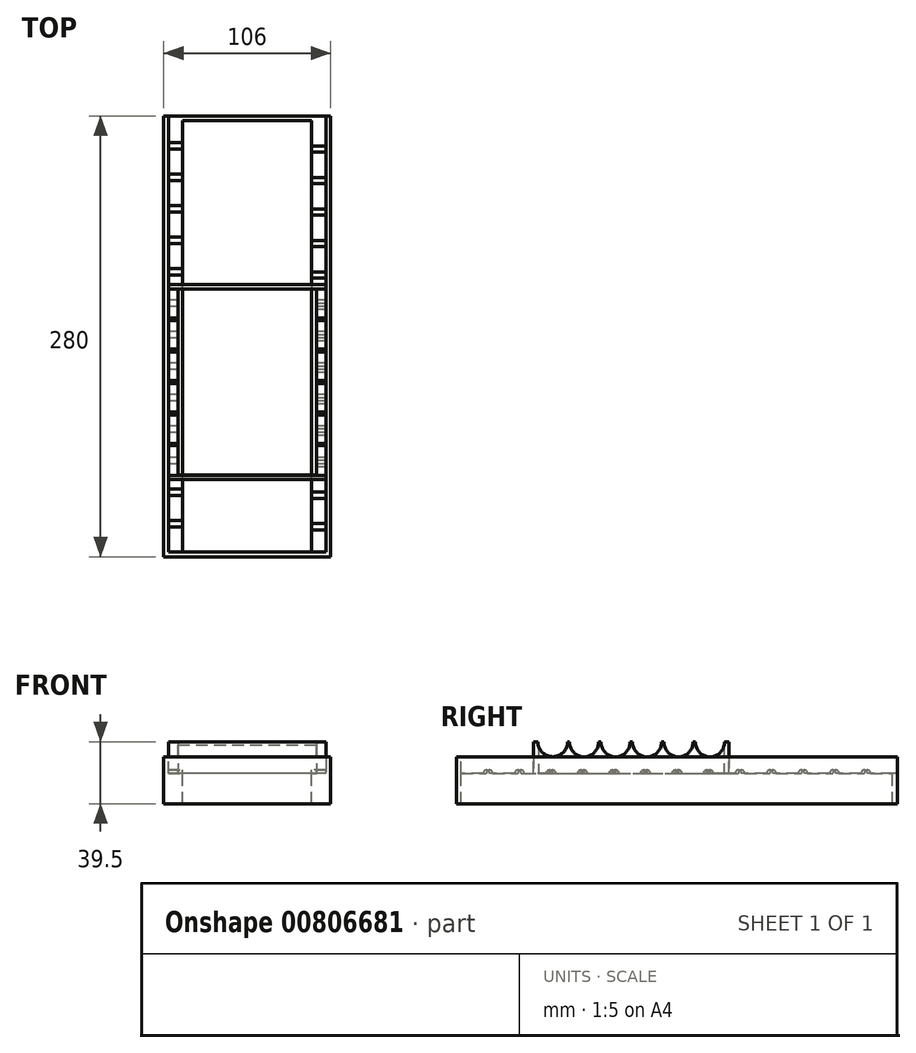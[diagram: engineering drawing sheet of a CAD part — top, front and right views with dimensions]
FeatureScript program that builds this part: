
annotation { "Feature Type Name" : "Feature", "Feature Type Description" : "" }
export const myFeature = defineFeature(function(context is Context, id is Id, definition is map)
    precondition{}
    {
        {
            var Q0;
            Q0=qCreatedBy(makeId("Top.planeOp"),FACE);
            var sketch = newSketch(context, id + "F0", { "sketchPlane" : qUnion([Q0])});
            skPoint(sketch, "E0.middle", {"position": v(0, 0) * mm});
            skLineSegment(sketch, "E1.bottom", {"start": v(-53, 140) * mm, "end": v(53, 140) * mm});
            skLineSegment(sketch, "E1.top", {"start": v(-53, -140) * mm, "end": v(53, -140) * mm});
            skLineSegment(sketch, "E1.left", {"start": v(-53, 140) * mm, "end": v(-53, -140) * mm});
            skLineSegment(sketch, "E1.right", {"start": v(53, 140) * mm, "end": v(53, -140) * mm});
            skSolve(sketch);
        }
        {
            var Q0;
            Q0 = qSketchRegion(id + "F0", true);
            extrude(context, id + "F1", {"entities" : qUnion([Q0]), "endBound" : BoundingType.SYMMETRIC, "depth" : 30 * mm, "offsetDistance" : 25 * mm});
        }
        {
            var Q0;
            Q0=makeQuery(id+"F1.opExtrude","CAP_FACE",FACE,{"disambiguationData":[OSD([sQuery(id+"F0.wireOp",EDGE,"E1.bottom"),sQuery(id+"F0.wireOp",EDGE,"E1.top"),sQuery(id+"F0.wireOp",EDGE,"E1.left"),sQuery(id+"F0.wireOp",EDGE,"E1.right")])],"isStart":false});
            var sketch = newSketch(context, id + "F2", { "sketchPlane" : qUnion([Q0])});
            skLineSegment(sketch, "E2.bottom", {"start": v(-41, 137) * mm, "end": v(41, 137) * mm});
            skLineSegment(sketch, "E2.top", {"start": v(-41, -137) * mm, "end": v(41, -137) * mm});
            skLineSegment(sketch, "E2.left", {"start": v(-41, 137) * mm, "end": v(-41, -137) * mm});
            skLineSegment(sketch, "E2.right", {"start": v(41, 137) * mm, "end": v(41, -137) * mm});
            skPoint(sketch, "E2.middle", {"position": v(0, 0) * mm});
            skSolve(sketch);
        }
        {
            var Q0;
            Q0=makeQuery(id+"F2.imprint","IMPRINT",FACE,{"disambiguationData":[TD([[makeQuery(id+"F2.imprint","IMPRINT",EDGE,{"derivedFrom":sQuery(id+"F2.wireOp",EDGE,"E2.bottom")}),-1.0]])]});
            extrude(context, id + "F3", {"entities" : qUnion([Q0]), "operationType" : NewBodyOperationType.REMOVE, "oppositeDirection" : true, "depth" : 39 * mm, "offsetDistance" : 25 * mm});
        }
        {
            var Q0;
            Q0=makeQuery(id+"F3.boolean.opBoolean","COPY",FACE,{"derivedFrom":makeQuery(id+"F3.opExtrude","SWEPT_FACE",FACE,{"disambiguationData":[OSD([sQuery(id+"F2.wireOp",EDGE,"E2.left")])]})});
            var sketch = newSketch(context, id + "F4", { "sketchPlane" : qUnion([Q0])});
            skLineSegment(sketch, "E3.bottom", {"start": v(-137, 15) * mm, "end": v(137, 15) * mm});
            skPoint(sketch, "E3.middle", {"position": v(0, 0) * mm});
            skLineSegment(sketch, "E4.left", {"start": v(-137, 15) * mm, "end": v(-137, 4.5) * mm});
            skLineSegment(sketch, "E4.right", {"start": v(137, 15) * mm, "end": v(137, 4.5) * mm});
            skLineSegment(sketch, "E5", {"start": v(-137, 4.5) * mm, "end": v(-121, 4.5) * mm});
            skArc(sketch, "E6", {"start": v(-117, 4.5) * mm, "mid": v(-119, 6.5) * mm, "end": v(-121, 4.5) * mm});
            skLineSegment(sketch, "E7", {"start": v(-117, 4.5) * mm, "end": v(-101, 4.5) * mm});
            skArc(sketch, "E8", {"start": v(-97, 4.5) * mm, "mid": v(-99, 6.5) * mm, "end": v(-101, 4.5) * mm});
            skLineSegment(sketch, "E9", {"start": v(-97, 4.5) * mm, "end": v(-81, 4.5) * mm});
            skArc(sketch, "E10", {"start": v(-77, 4.5) * mm, "mid": v(-79, 6.5) * mm, "end": v(-81, 4.5) * mm});
            skLineSegment(sketch, "E11", {"start": v(-77, 4.5) * mm, "end": v(-61, 4.5) * mm});
            skArc(sketch, "E12", {"start": v(-57, 4.5) * mm, "mid": v(-59, 6.5) * mm, "end": v(-61, 4.5) * mm});
            skLineSegment(sketch, "E13", {"start": v(-57, 4.5) * mm, "end": v(-41, 4.5) * mm});
            skArc(sketch, "E14", {"start": v(-37, 4.5) * mm, "mid": v(-39, 6.5) * mm, "end": v(-41, 4.5) * mm});
            skLineSegment(sketch, "E15", {"start": v(-37, 4.5) * mm, "end": v(-21, 4.5) * mm});
            skArc(sketch, "E16", {"start": v(-17, 4.5) * mm, "mid": v(-19, 6.5) * mm, "end": v(-21, 4.5) * mm});
            skLineSegment(sketch, "E17", {"start": v(-17, 4.5) * mm, "end": v(-1, 4.5) * mm});
            skArc(sketch, "E18", {"start": v(3, 4.5) * mm, "mid": v(1, 6.5) * mm, "end": v(-1, 4.5) * mm});
            skLineSegment(sketch, "E19", {"start": v(3, 4.5) * mm, "end": v(19, 4.5) * mm});
            skArc(sketch, "E20", {"start": v(23, 4.5) * mm, "mid": v(21, 6.5) * mm, "end": v(19, 4.5) * mm});
            skLineSegment(sketch, "E21", {"start": v(23, 4.5) * mm, "end": v(39, 4.5) * mm});
            skArc(sketch, "E22", {"start": v(43, 4.5) * mm, "mid": v(41, 6.5) * mm, "end": v(39, 4.5) * mm});
            skLineSegment(sketch, "E23", {"start": v(43, 4.5) * mm, "end": v(59, 4.5) * mm});
            skArc(sketch, "E24", {"start": v(63, 4.5) * mm, "mid": v(61, 6.5) * mm, "end": v(59, 4.5) * mm});
            skLineSegment(sketch, "E25", {"start": v(63, 4.5) * mm, "end": v(79, 4.5) * mm});
            skArc(sketch, "E26", {"start": v(83, 4.5) * mm, "mid": v(81, 6.5) * mm, "end": v(79, 4.5) * mm});
            skLineSegment(sketch, "E27", {"start": v(83, 4.5) * mm, "end": v(99, 4.5) * mm});
            skArc(sketch, "E28", {"start": v(103, 4.5) * mm, "mid": v(101, 6.5) * mm, "end": v(99, 4.5) * mm});
            skLineSegment(sketch, "E29", {"start": v(103, 4.5) * mm, "end": v(119, 4.5) * mm});
            skArc(sketch, "E30", {"start": v(123, 4.5) * mm, "mid": v(121, 6.5) * mm, "end": v(119, 4.5) * mm});
            skLineSegment(sketch, "E31", {"start": v(123, 4.5) * mm, "end": v(137, 4.5) * mm});
            skSolve(sketch);
        }
        {
            var Q0;
            Q0=makeQuery(id+"F3.boolean.opBoolean","COPY",FACE,{"derivedFrom":makeQuery(id+"F3.opExtrude","SWEPT_FACE",FACE,{"disambiguationData":[OSD([sQuery(id+"F2.wireOp",EDGE,"E2.right")])]})});
            var sketch = newSketch(context, id + "F5", { "sketchPlane" : qUnion([Q0])});
            skLineSegment(sketch, "E32.top", {"start": v(137, 15) * mm, "end": v(-137, 15) * mm});
            skLineSegment(sketch, "E33.bottom", {"start": v(-137, 15) * mm, "end": v(137, 15) * mm});
            skPoint(sketch, "E33.middle", {"position": v(0, 0) * mm});
            skLineSegment(sketch, "E34.left", {"start": v(-137, 15) * mm, "end": v(-137, 4.5) * mm});
            skLineSegment(sketch, "E34.right", {"start": v(137, 15) * mm, "end": v(137, 4.5) * mm});
            skLineSegment(sketch, "E35", {"start": v(-137, 4.5) * mm, "end": v(-121, 4.5) * mm});
            skArc(sketch, "E36", {"start": v(-117, 4.5) * mm, "mid": v(-119, 6.5) * mm, "end": v(-121, 4.5) * mm});
            skLineSegment(sketch, "E37", {"start": v(-117, 4.5) * mm, "end": v(-101, 4.5) * mm});
            skArc(sketch, "E38", {"start": v(-97, 4.5) * mm, "mid": v(-99, 6.5) * mm, "end": v(-101, 4.5) * mm});
            skLineSegment(sketch, "E39", {"start": v(-97, 4.5) * mm, "end": v(-81, 4.5) * mm});
            skArc(sketch, "E40", {"start": v(-77, 4.5) * mm, "mid": v(-79, 6.5) * mm, "end": v(-81, 4.5) * mm});
            skLineSegment(sketch, "E41", {"start": v(-77, 4.5) * mm, "end": v(-61, 4.5) * mm});
            skArc(sketch, "E42", {"start": v(-57, 4.5) * mm, "mid": v(-59, 6.5) * mm, "end": v(-61, 4.5) * mm});
            skLineSegment(sketch, "E43", {"start": v(-57, 4.5) * mm, "end": v(-41, 4.5) * mm});
            skArc(sketch, "E44", {"start": v(-37, 4.5) * mm, "mid": v(-39, 6.5) * mm, "end": v(-41, 4.5) * mm});
            skLineSegment(sketch, "E45", {"start": v(-37, 4.5) * mm, "end": v(-21, 4.5) * mm});
            skArc(sketch, "E46", {"start": v(-17, 4.5) * mm, "mid": v(-19, 6.5) * mm, "end": v(-21, 4.5) * mm});
            skLineSegment(sketch, "E47", {"start": v(-17, 4.5) * mm, "end": v(-1, 4.5) * mm});
            skArc(sketch, "E48", {"start": v(3, 4.5) * mm, "mid": v(1, 6.5) * mm, "end": v(-1, 4.5) * mm});
            skLineSegment(sketch, "E49", {"start": v(3, 4.5) * mm, "end": v(19, 4.5) * mm});
            skArc(sketch, "E50", {"start": v(23, 4.5) * mm, "mid": v(21, 6.5) * mm, "end": v(19, 4.5) * mm});
            skLineSegment(sketch, "E51", {"start": v(23, 4.5) * mm, "end": v(39, 4.5) * mm});
            skArc(sketch, "E52", {"start": v(43, 4.5) * mm, "mid": v(41, 6.5) * mm, "end": v(39, 4.5) * mm});
            skLineSegment(sketch, "E53", {"start": v(43, 4.5) * mm, "end": v(59, 4.5) * mm});
            skArc(sketch, "E54", {"start": v(63, 4.5) * mm, "mid": v(61, 6.5) * mm, "end": v(59, 4.5) * mm});
            skLineSegment(sketch, "E55", {"start": v(63, 4.5) * mm, "end": v(79, 4.5) * mm});
            skArc(sketch, "E56", {"start": v(83, 4.5) * mm, "mid": v(81, 6.5) * mm, "end": v(79, 4.5) * mm});
            skLineSegment(sketch, "E57", {"start": v(83, 4.5) * mm, "end": v(99, 4.5) * mm});
            skArc(sketch, "E58", {"start": v(103, 4.5) * mm, "mid": v(101, 6.5) * mm, "end": v(99, 4.5) * mm});
            skLineSegment(sketch, "E59", {"start": v(103, 4.5) * mm, "end": v(119, 4.5) * mm});
            skArc(sketch, "E60", {"start": v(123, 4.5) * mm, "mid": v(121, 6.5) * mm, "end": v(119, 4.5) * mm});
            skLineSegment(sketch, "E61", {"start": v(123, 4.5) * mm, "end": v(137, 4.5) * mm});
            skPoint(sketch, "E62.middle", {"position": v(0.81, 5.86) * mm});
            skSolve(sketch);
        }
        {
            var Q0;
            Q0 = qSketchRegion(id + "F4", true);
            extrude(context, id + "F6", {"entities" : qUnion([Q0]), "operationType" : NewBodyOperationType.REMOVE, "oppositeDirection" : true, "depth" : 9 * mm, "offsetDistance" : 25 * mm});
        }
        {
            var Q0;
            {var subQ2=sQuery(id+"F5.wireOp",EDGE,"E32.top");Q0=makeQuery(id+"F5.imprint","IMPRINT",FACE,{"disambiguationData":[TD([[makeQuery(id+"F5.imprint","IMPRINT",EDGE,{"derivedFrom":subQ2}),-1.0]])]});}
            extrude(context, id + "F7", {"entities" : qUnion([Q0]), "operationType" : NewBodyOperationType.REMOVE, "oppositeDirection" : true, "depth" : 9 * mm, "offsetDistance" : 25 * mm});
        }
        {
            var Q0;
            Q0=makeQuery(id+"F7.boolean.opBoolean","MERGE",FACE,{"derivedFrom":[makeQuery(id+"F6.boolean.opBoolean","MERGE",FACE,{"derivedFrom":[makeQuery(id+"F3.boolean.opBoolean","COPY",FACE,{"derivedFrom":makeQuery(id+"F3.opExtrude","SWEPT_FACE",FACE,{"disambiguationData":[OSD([sQuery(id+"F2.wireOp",EDGE,"E2.bottom")])]})}),makeQuery(id+"F6.opExtrude","SWEPT_FACE",FACE,{"disambiguationData":[OSD([sQuery(id+"F4.wireOp",EDGE,"E4.right")])]})]}),makeQuery(id+"F7.opExtrude","SWEPT_FACE",FACE,{"disambiguationData":[OSD([sQuery(id+"F5.wireOp",EDGE,"E34.left")])]})]});
            var sketch = newSketch(context, id + "F8", { "sketchPlane" : qUnion([Q0])});
            skLineSegment(sketch, "E63", {"start": v(-50, 15) * mm, "end": v(-50, 4.5) * mm});
            skLineSegment(sketch, "E64", {"start": v(-50, 4.5) * mm, "end": v(50, 4.5) * mm});
            skLineSegment(sketch, "E65", {"start": v(50, 4.5) * mm, "end": v(50, 15) * mm});
            skLineSegment(sketch, "E66", {"start": v(50, 15) * mm, "end": v(-50, 15) * mm});
            skSolve(sketch);
        }
        {
            var Q0;
            Q0 = qSketchRegion(id + "F8", true);
            extrude(context, id + "F9", {"entities" : qUnion([Q0]), "operationType" : NewBodyOperationType.REMOVE, "oppositeDirection" : true, "depth" : 25 * mm, "offsetDistance" : 25 * mm});
        }
        {
            var Q0;
            Q0=makeQuery(id+"F9.boolean.opBoolean","MERGE",FACE,{"derivedFrom":[makeQuery(id+"F6.boolean.opBoolean","COPY",FACE,{"derivedFrom":makeQuery(id+"F6.opExtrude","CAP_FACE",FACE,{"disambiguationData":[OSD([sQuery(id+"F4.wireOp",EDGE,"E3.bottom"),sQuery(id+"F4.wireOp",EDGE,"E4.left"),sQuery(id+"F4.wireOp",EDGE,"E4.right"),sQuery(id+"F4.wireOp",EDGE,"E5"),sQuery(id+"F4.wireOp",EDGE,"E6"),sQuery(id+"F4.wireOp",EDGE,"E7"),sQuery(id+"F4.wireOp",EDGE,"E8"),sQuery(id+"F4.wireOp",EDGE,"E9"),sQuery(id+"F4.wireOp",EDGE,"E10"),sQuery(id+"F4.wireOp",EDGE,"E11"),sQuery(id+"F4.wireOp",EDGE,"E12"),sQuery(id+"F4.wireOp",EDGE,"E13"),sQuery(id+"F4.wireOp",EDGE,"E14"),sQuery(id+"F4.wireOp",EDGE,"E15"),sQuery(id+"F4.wireOp",EDGE,"E16"),sQuery(id+"F4.wireOp",EDGE,"E17"),sQuery(id+"F4.wireOp",EDGE,"E18"),sQuery(id+"F4.wireOp",EDGE,"E19"),sQuery(id+"F4.wireOp",EDGE,"E20"),sQuery(id+"F4.wireOp",EDGE,"E21"),sQuery(id+"F4.wireOp",EDGE,"E22"),sQuery(id+"F4.wireOp",EDGE,"E23"),sQuery(id+"F4.wireOp",EDGE,"E24"),sQuery(id+"F4.wireOp",EDGE,"E25"),sQuery(id+"F4.wireOp",EDGE,"E26"),sQuery(id+"F4.wireOp",EDGE,"E27"),sQuery(id+"F4.wireOp",EDGE,"E28"),sQuery(id+"F4.wireOp",EDGE,"E29"),sQuery(id+"F4.wireOp",EDGE,"E30"),sQuery(id+"F4.wireOp",EDGE,"E31")])],"isStart":false})}),makeQuery(id+"F9.opExtrude","SWEPT_FACE",FACE,{"disambiguationData":[OSD([sQuery(id+"F8.wireOp",EDGE,"E63")])]})]});
            var sketch = newSketch(context, id + "F10", { "sketchPlane" : qUnion([Q0])});
            skPoint(sketch, "E67.middle", {"position": v(-29, 14.5) * mm});
            skArc(sketch, "E68", {"start": v(-77, 4.5) * mm, "mid": v(-79, 6.49) * mm, "end": v(-81, 4.5) * mm});
            skArc(sketch, "E69", {"start": v(-57, 4.5) * mm, "mid": v(-59, 6.46) * mm, "end": v(-61, 4.5) * mm});
            skArc(sketch, "E70", {"start": v(-37, 4.5) * mm, "mid": v(-39, 6.54) * mm, "end": v(-41, 4.5) * mm});
            skArc(sketch, "E71", {"start": v(-17, 4.5) * mm, "mid": v(-19, 6.47) * mm, "end": v(-21, 4.5) * mm});
            skArc(sketch, "E72", {"start": v(3, 4.5) * mm, "mid": v(1, 6.53) * mm, "end": v(-1, 4.5) * mm});
            skArc(sketch, "E73", {"start": v(23, 4.5) * mm, "mid": v(21, 6.51) * mm, "end": v(19, 4.5) * mm});
            skArc(sketch, "E74", {"start": v(-88.32, 24.5) * mm, "mid": v(-78.85, 15.04) * mm, "end": v(-69.39, 24.5) * mm});
            skArc(sketch, "E75", {"start": v(-68.2, 24.5) * mm, "mid": v(-59, 14.9) * mm, "end": v(-49.8, 24.5) * mm});
            skLineSegment(sketch, "E76", {"start": v(-69.39, 24.5) * mm, "end": v(-68.2, 24.5) * mm});
            skArc(sketch, "E77", {"start": v(-48.2, 24.5) * mm, "mid": v(-39, 14.9) * mm, "end": v(-29.8, 24.5) * mm});
            skArc(sketch, "E78", {"start": v(-28.2, 24.5) * mm, "mid": v(-19, 14.9) * mm, "end": v(-9.8, 24.5) * mm});
            skArc(sketch, "E79", {"start": v(-8.2, 24.5) * mm, "mid": v(1, 14.9) * mm, "end": v(10.2, 24.5) * mm});
            skArc(sketch, "E80", {"start": v(11.8, 24.5) * mm, "mid": v(21, 14.9) * mm, "end": v(30.2, 24.5) * mm});
            skLineSegment(sketch, "E81", {"start": v(-49.8, 24.5) * mm, "end": v(-48.2, 24.5) * mm});
            skLineSegment(sketch, "E82", {"start": v(-29.8, 24.5) * mm, "end": v(-28.2, 24.5) * mm});
            skLineSegment(sketch, "E83", {"start": v(-9.8, 24.5) * mm, "end": v(-8.2, 24.5) * mm});
            skLineSegment(sketch, "E84", {"start": v(10.2, 24.5) * mm, "end": v(11.8, 24.5) * mm});
            skLineSegment(sketch, "E85", {"start": v(-88.32, 24.5) * mm, "end": v(-89.92, 24.5) * mm});
            skLineSegment(sketch, "E86", {"start": v(30.2, 24.5) * mm, "end": v(31.8, 24.5) * mm});
            skLineSegment(sketch, "E87", {"start": v(-77, 4.5) * mm, "end": v(-61, 4.5) * mm});
            skLineSegment(sketch, "E88", {"start": v(-57, 4.5) * mm, "end": v(-41, 4.5) * mm});
            skLineSegment(sketch, "E89", {"start": v(-37, 4.5) * mm, "end": v(-21, 4.5) * mm});
            skLineSegment(sketch, "E90", {"start": v(-17, 4.5) * mm, "end": v(-1, 4.5) * mm});
            skLineSegment(sketch, "E91", {"start": v(3, 4.5) * mm, "end": v(19, 4.5) * mm});
            skLineSegment(sketch, "E92", {"start": v(-81, 4.5) * mm, "end": v(-91, 4.5) * mm});
            skLineSegment(sketch, "E93", {"start": v(-91, 4.5) * mm, "end": v(-91, 24.5) * mm});
            skLineSegment(sketch, "E94", {"start": v(-91, 24.5) * mm, "end": v(-89.92, 24.5) * mm});
            skLineSegment(sketch, "E95", {"start": v(23, 4.5) * mm, "end": v(33, 4.5) * mm});
            skLineSegment(sketch, "E96", {"start": v(33, 4.5) * mm, "end": v(33, 24.5) * mm});
            skLineSegment(sketch, "E97", {"start": v(33, 24.5) * mm, "end": v(31.8, 24.5) * mm});
            skSolve(sketch);
        }
        {
            var Q0;
            Q0 = qSketchRegion(id + "F10", true);
            var Q1;
            Q1=makeQuery(id+"F9.boolean.opBoolean","MERGE",FACE,{"derivedFrom":[makeQuery(id+"F7.boolean.opBoolean","COPY",FACE,{"derivedFrom":makeQuery(id+"F7.opExtrude","CAP_FACE",FACE,{"disambiguationData":[OSD([sQuery(id+"F5.wireOp",EDGE,"E32.top"),sQuery(id+"F5.wireOp",EDGE,"E34.left"),sQuery(id+"F5.wireOp",EDGE,"E34.right"),sQuery(id+"F5.wireOp",EDGE,"E35"),sQuery(id+"F5.wireOp",EDGE,"E36"),sQuery(id+"F5.wireOp",EDGE,"E37"),sQuery(id+"F5.wireOp",EDGE,"E38"),sQuery(id+"F5.wireOp",EDGE,"E39"),sQuery(id+"F5.wireOp",EDGE,"E40"),sQuery(id+"F5.wireOp",EDGE,"E41"),sQuery(id+"F5.wireOp",EDGE,"E42"),sQuery(id+"F5.wireOp",EDGE,"E43"),sQuery(id+"F5.wireOp",EDGE,"E44"),sQuery(id+"F5.wireOp",EDGE,"E45"),sQuery(id+"F5.wireOp",EDGE,"E46"),sQuery(id+"F5.wireOp",EDGE,"E47"),sQuery(id+"F5.wireOp",EDGE,"E48"),sQuery(id+"F5.wireOp",EDGE,"E49"),sQuery(id+"F5.wireOp",EDGE,"E50"),sQuery(id+"F5.wireOp",EDGE,"E51"),sQuery(id+"F5.wireOp",EDGE,"E52"),sQuery(id+"F5.wireOp",EDGE,"E53"),sQuery(id+"F5.wireOp",EDGE,"E54"),sQuery(id+"F5.wireOp",EDGE,"E55"),sQuery(id+"F5.wireOp",EDGE,"E56"),sQuery(id+"F5.wireOp",EDGE,"E57"),sQuery(id+"F5.wireOp",EDGE,"E58"),sQuery(id+"F5.wireOp",EDGE,"E59"),sQuery(id+"F5.wireOp",EDGE,"E60"),sQuery(id+"F5.wireOp",EDGE,"E61")])],"isStart":false})}),makeQuery(id+"F9.opExtrude","SWEPT_FACE",FACE,{"disambiguationData":[OSD([sQuery(id+"F8.wireOp",EDGE,"E65")])]})]});
            extrude(context, id + "F11", {"entities" : qUnion([Q0]), "endBound" : BoundingType.UP_TO_SURFACE, "depth" : 25 * mm, "endBoundEntityFace" : qUnion([Q1]), "offsetDistance" : 25 * mm});
        }
        {
            var Q0;
            Q0=makeQuery(id+"F11.opExtrude","SWEPT_FACE",FACE,{"disambiguationData":[OSD([sQuery(id+"F10.wireOp",EDGE,"E92")])]});
            var sketch = newSketch(context, id + "F12", { "sketchPlane" : qUnion([Q0])});
            skLineSegment(sketch, "E98", {"start": v(-44, 86) * mm, "end": v(-44, -30) * mm});
            skLineSegment(sketch, "E99", {"start": v(44, 86) * mm, "end": v(44, -30) * mm});
            skLineSegment(sketch, "E100", {"start": v(44, -30) * mm, "end": v(-44, -30) * mm});
            skLineSegment(sketch, "E101", {"start": v(44, 88) * mm, "end": v(-44, 88) * mm});
            skLineSegment(sketch, "E102", {"start": v(-44, 86) * mm, "end": v(-44, 88) * mm});
            skLineSegment(sketch, "E103", {"start": v(44, 86) * mm, "end": v(44, 88) * mm});
            skSolve(sketch);
        }
        {
            var Q0;
            {var subQ0=sQuery(id+"F12.wireOp",EDGE,"E100");Q0=makeQuery(id+"F12.imprint","IMPRINT",FACE,{"disambiguationData":[TD([[makeQuery(id+"F12.imprint","IMPRINT",EDGE,{"derivedFrom":subQ0}),-1.0]])]});}
            var Q1;
            Q1=makeQuery(id+"F12.imprint","IMPRINT",FACE,{"disambiguationData":[TD([[makeQuery(id+"F12.imprint","IMPRINT",EDGE,{"derivedFrom":sQuery(id+"F12.wireOp",EDGE,"E101")}),1.0]])]});
            extrude(context, id + "F13", {"entities" : qUnion([Q0, Q1]), "operationType" : NewBodyOperationType.REMOVE, "oppositeDirection" : true, "depth" : 25 * mm, "offsetDistance" : 25 * mm});
        }
    });
